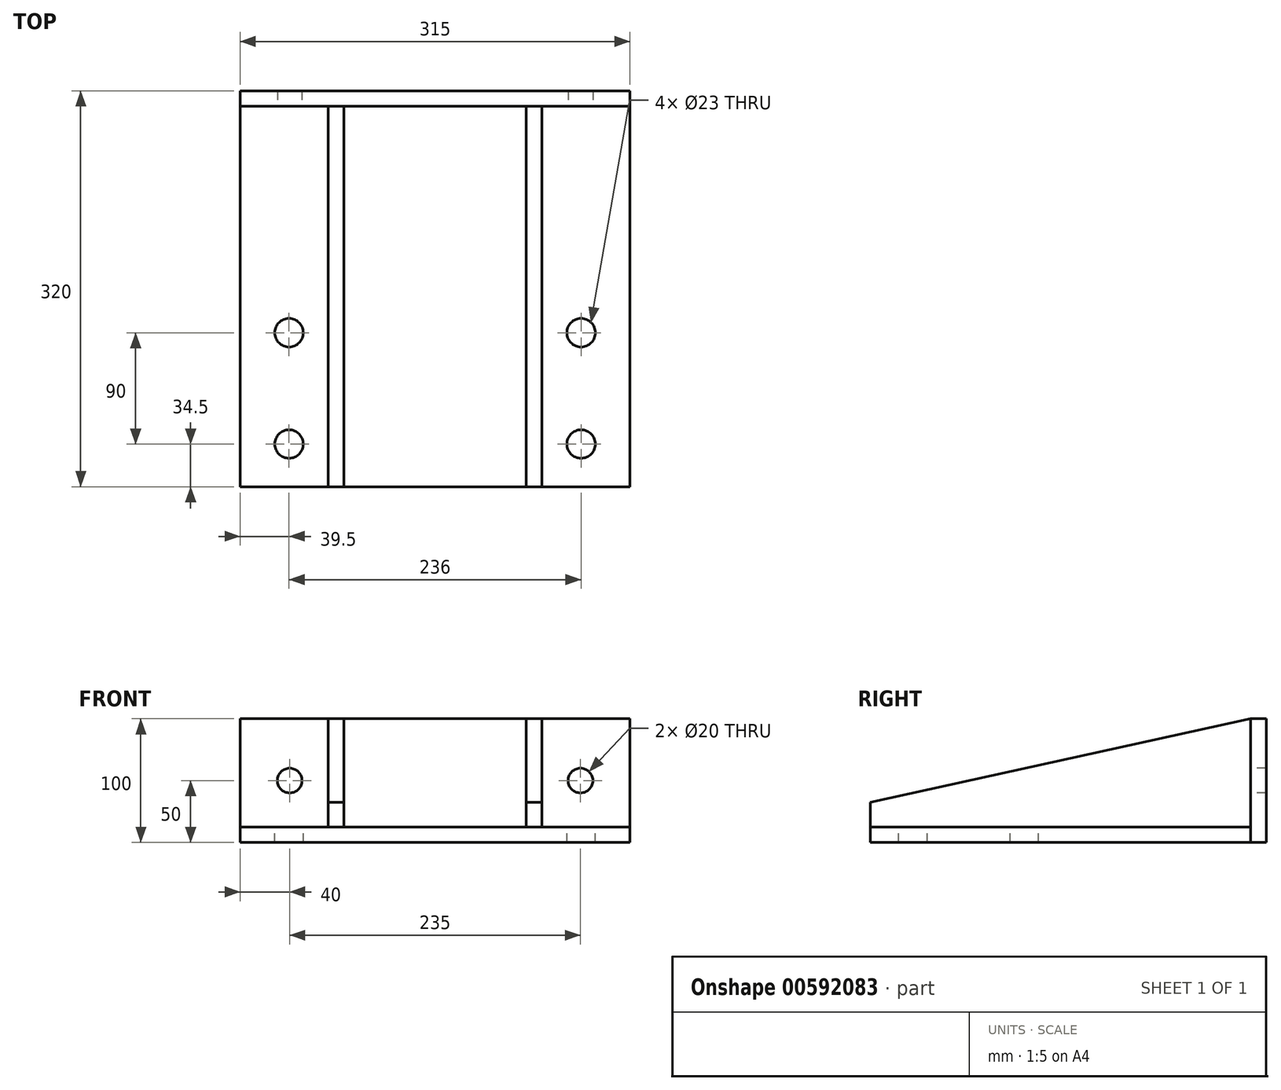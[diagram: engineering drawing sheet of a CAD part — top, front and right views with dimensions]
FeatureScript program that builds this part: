
annotation { "Feature Type Name" : "Feature", "Feature Type Description" : "" }
export const myFeature = defineFeature(function(context is Context, id is Id, definition is map)
    precondition{}
    {
        {
            var Q0;
            Q0=qCreatedBy(makeId("Top.planeOp"),FACE);
            var sketch = newSketch(context, id + "F0", { "sketchPlane" : qUnion([Q0])});
            skLineSegment(sketch, "E0.bottom", {"start": v(-157.5, 153.75) * mm, "end": v(157.5, 153.75) * mm});
            skLineSegment(sketch, "E0.top", {"start": v(-157.5, -153.75) * mm, "end": v(157.5, -153.75) * mm});
            skLineSegment(sketch, "E0.left", {"start": v(-157.5, 153.75) * mm, "end": v(-157.5, -153.75) * mm});
            skLineSegment(sketch, "E0.right", {"start": v(157.5, 153.75) * mm, "end": v(157.5, -153.75) * mm});
            skLineSegment(sketch, "E1", {"start": v(0, 153.75) * mm, "end": v(0, -153.75) * mm, "construction": true});
            skLineSegment(sketch, "E2", {"start": v(-157.5, 0) * mm, "end": v(157.5, 0) * mm, "construction": true});
            skSolve(sketch);
        }
        {
            var Q0;
            Q0=makeQuery(id+"F0.imprint","IMPRINT",FACE,{"disambiguationData":[TD([[makeQuery(id+"F0.imprint","IMPRINT",EDGE,{"derivedFrom":sQuery(id+"F0.wireOp",EDGE,"E0.bottom")}),-1.0]])]});
            extrude(context, id + "F1", {"entities" : qUnion([Q0]), "depth" : 12.5 * mm, "offsetDistance" : 25 * mm});
        }
        {
            var Q0;
            Q0=makeQuery(id+"F1.opExtrude","SWEPT_FACE",FACE,{"disambiguationData":[OSD([sQuery(id+"F0.wireOp",EDGE,"E0.bottom")])]});
            var sketch = newSketch(context, id + "F2", { "sketchPlane" : qUnion([Q0])});
            skLineSegment(sketch, "E3.bottom", {"start": v(-157.5, 0) * mm, "end": v(157.5, 0) * mm});
            skLineSegment(sketch, "E3.top", {"start": v(-157.5, 100) * mm, "end": v(157.5, 100) * mm});
            skLineSegment(sketch, "E3.left", {"start": v(-157.5, 0) * mm, "end": v(-157.5, 100) * mm});
            skLineSegment(sketch, "E3.right", {"start": v(157.5, 0) * mm, "end": v(157.5, 100) * mm});
            skSolve(sketch);
        }
        {
            var Q0;
            Q0 = qSketchRegion(id + "F2", true);
            extrude(context, id + "F3", {"entities" : qUnion([Q0]), "depth" : 12.5 * mm, "offsetDistance" : 25 * mm});
        }
        {
            var Q0;
            Q0=qCreatedBy(makeId("Right.planeOp"),FACE);
            var sketch = newSketch(context, id + "F4", { "sketchPlane" : qUnion([Q0])});
            skLineSegment(sketch, "E4", {"start": v(-153.75, 12.5) * mm, "end": v(-153.75, 32.5) * mm});
            skLineSegment(sketch, "E5", {"start": v(-153.75, 32.5) * mm, "end": v(153.75, 100) * mm});
            skLineSegment(sketch, "E6", {"start": v(153.75, 100) * mm, "end": v(153.75, 12.5) * mm});
            skLineSegment(sketch, "E7", {"start": v(153.75, 12.5) * mm, "end": v(-153.75, 12.5) * mm});
            skSolve(sketch);
        }
        {
            var Q0;
            Q0=qCreatedBy(makeId("Right.planeOp"),FACE);
            cPlane(context, id + "F5", {"entities" : qUnion([Q0]), "cplaneType" : CPlaneType.OFFSET, "offset" : 80 * mm, "width" : 150 * mm, "height" : 150 * mm});
        }
        {
            var Q0;
            Q0=qCreatedBy(makeId("Right.planeOp"),FACE);
            cPlane(context, id + "F6", {"entities" : qUnion([Q0]), "cplaneType" : CPlaneType.OFFSET, "offset" : 80 * mm, "oppositeDirection" : true, "width" : 150 * mm, "height" : 150 * mm});
        }
        {
            var Q0;
            Q0=qCreatedBy(id+"F6.planeOp",FACE);
            var sketch = newSketch(context, id + "F7", { "sketchPlane" : qUnion([Q0])});
            skLineSegment(sketch, "E8", {"start": v(-153.75, 12.5) * mm, "end": v(-153.75, 32.5) * mm});
            skLineSegment(sketch, "E9", {"start": v(-153.75, 32.5) * mm, "end": v(153.75, 100) * mm});
            skLineSegment(sketch, "E10", {"start": v(153.75, 100) * mm, "end": v(153.75, 12.5) * mm});
            skLineSegment(sketch, "E11", {"start": v(153.75, 12.5) * mm, "end": v(-153.75, 12.5) * mm});
            skSolve(sketch);
        }
        {
            var Q0;
            Q0=qCreatedBy(id+"F5.planeOp",FACE);
            var sketch = newSketch(context, id + "F8", { "sketchPlane" : qUnion([Q0])});
            skLineSegment(sketch, "E12", {"start": v(-153.75, 12.5) * mm, "end": v(-153.75, 32.5) * mm});
            skLineSegment(sketch, "E13", {"start": v(-153.75, 32.5) * mm, "end": v(153.75, 100) * mm});
            skLineSegment(sketch, "E14", {"start": v(153.75, 100) * mm, "end": v(153.75, 12.5) * mm});
            skLineSegment(sketch, "E15", {"start": v(153.75, 12.5) * mm, "end": v(-153.75, 12.5) * mm});
            skSolve(sketch);
        }
        {
            var Q0;
            Q0 = qSketchRegion(id + "F7", true);
            var Q1;
            Q1 = qSketchRegion(id + "F8", true);
            extrude(context, id + "F9", {"entities" : qUnion([Q0, Q1]), "endBound" : BoundingType.SYMMETRIC, "depth" : 12.5 * mm, "offsetDistance" : 25 * mm});
        }
        {
            var Q0;
            Q0=makeQuery(id+"F3.opExtrude","CAP_FACE",FACE,{"disambiguationData":[OSD([sQuery(id+"F2.wireOp",EDGE,"E3.bottom"),sQuery(id+"F2.wireOp",EDGE,"E3.top"),sQuery(id+"F2.wireOp",EDGE,"E3.left"),sQuery(id+"F2.wireOp",EDGE,"E3.right")])],"isStart":true});
            var sketch = newSketch(context, id + "F10", { "sketchPlane" : qUnion([Q0])});
            skCircle(sketch, "E16", {"center": v(117.5, 50) * mm, "radius": 10 * mm});
            skCircle(sketch, "E17.MirrorC", {"center": v(-117.5, 50) * mm, "radius": 10 * mm});
            skSolve(sketch);
        }
        {
            var Q0;
            Q0 = qSketchRegion(id + "F10", true);
            extrude(context, id + "F11", {"entities" : qUnion([Q0]), "operationType" : NewBodyOperationType.REMOVE, "endBound" : BoundingType.UP_TO_NEXT, "oppositeDirection" : true, "depth" : 25 * mm, "offsetDistance" : 25 * mm});
        }
        {
            var Q0;
            Q0=makeQuery(id+"F1.opExtrude","CAP_FACE",FACE,{"disambiguationData":[OSD([sQuery(id+"F0.wireOp",EDGE,"E0.bottom"),sQuery(id+"F0.wireOp",EDGE,"E0.top"),sQuery(id+"F0.wireOp",EDGE,"E0.left"),sQuery(id+"F0.wireOp",EDGE,"E0.right")])],"isStart":false});
            var sketch = newSketch(context, id + "F12", { "sketchPlane" : qUnion([Q0])});
            skCircle(sketch, "E18", {"center": v(-118, -119.25) * mm, "radius": 11.5 * mm});
            skCircle(sketch, "E19", {"center": v(-118, -29.25) * mm, "radius": 11.5 * mm});
            skLineSegment(sketch, "E20", {"start": v(-118, -29.25) * mm, "end": v(-118, -153.75) * mm});
            skCircle(sketch, "E21.MirrorC", {"center": v(118, -29.25) * mm, "radius": 11.5 * mm});
            skCircle(sketch, "E22.MirrorC", {"center": v(118, -119.25) * mm, "radius": 11.5 * mm});
            skSolve(sketch);
        }
        {
            var Q0;
            Q0 = qSketchRegion(id + "F12", true);
            extrude(context, id + "F13", {"entities" : qUnion([Q0]), "operationType" : NewBodyOperationType.REMOVE, "endBound" : BoundingType.UP_TO_NEXT, "oppositeDirection" : true, "depth" : 25 * mm, "offsetDistance" : 25 * mm});
        }
    });
